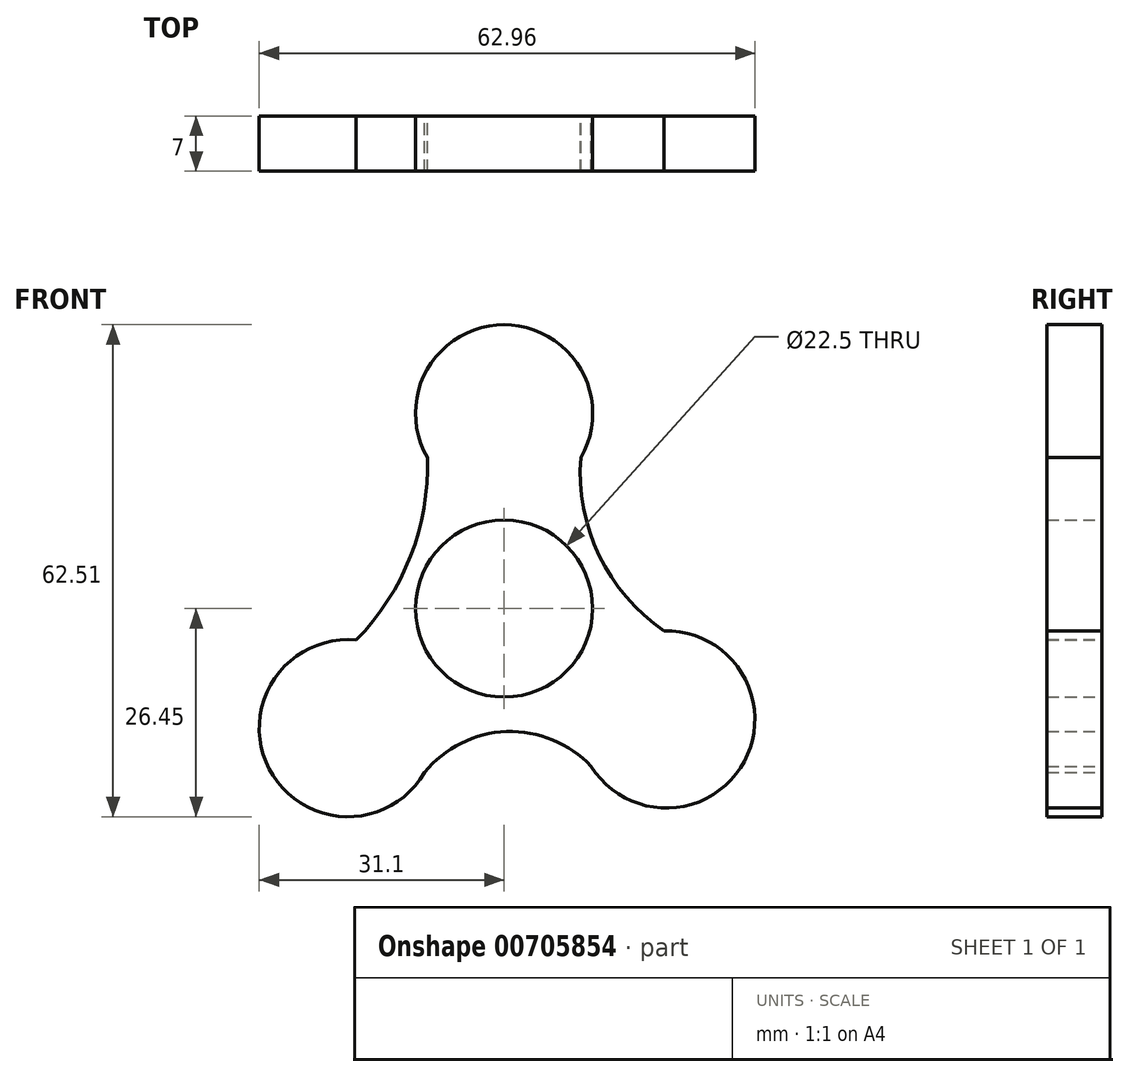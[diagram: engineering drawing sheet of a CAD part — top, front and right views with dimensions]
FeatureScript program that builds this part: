
annotation { "Feature Type Name" : "Feature", "Feature Type Description" : "" }
export const myFeature = defineFeature(function(context is Context, id is Id, definition is map)
    precondition{}
    {
        {
            var Q0;
            Q0=qCreatedBy(makeId("Front.planeOp"),FACE);
            var sketch = newSketch(context, id + "F0", { "sketchPlane" : qUnion([Q0])});
            skCircle(sketch, "E0", {"center": v(0, 0) * mm, "radius": 11.25 * mm});
            skCircle(sketch, "E1", {"center": v(0, 24.8) * mm, "radius": 11.25 * mm});
            skCircle(sketch, "E2", {"center": v(20.6, -14.08) * mm, "radius": 11.25 * mm});
            skCircle(sketch, "E3", {"center": v(-19.85, -15.2) * mm, "radius": 11.25 * mm});
            skLineSegment(sketch, "E4", {"start": v(0, 24.8) * mm, "end": v(0, 41.12) * mm});
            skLineSegment(sketch, "E5", {"start": v(0, 24.8) * mm, "end": v(17.45, 14.73) * mm});
            skLineSegment(sketch, "E6", {"start": v(0, 24.8) * mm, "end": v(-15.27, 15.99) * mm});
            skLineSegment(sketch, "E7", {"start": v(-19.85, -15.2) * mm, "end": v(-19.85, 5.14) * mm});
            skLineSegment(sketch, "E8", {"start": v(-19.85, -15.2) * mm, "end": v(-37.06, -28.16) * mm});
            skLineSegment(sketch, "E9", {"start": v(-19.85, -15.2) * mm, "end": v(-4.02, -24.34) * mm});
            skLineSegment(sketch, "E10", {"start": v(20.6, -14.08) * mm, "end": v(20.6, 8.04) * mm});
            skLineSegment(sketch, "E11", {"start": v(20.6, -14.08) * mm, "end": v(38.26, -24.28) * mm});
            skLineSegment(sketch, "E12", {"start": v(20.6, -14.08) * mm, "end": v(7.87, -26.6) * mm});
            skArc(sketch, "E13", {"start": v(-19.85, -5.03) * mm, "mid": v(-12.16, 5.97) * mm, "end": v(-9.74, 19.18) * mm});
            skArc(sketch, "E14", {"start": v(9.74, 19.18) * mm, "mid": v(12.16, 6.6) * mm, "end": v(20.6, -3.02) * mm});
            skArc(sketch, "E15", {"start": v(12.58, -21.97) * mm, "mid": v(1.53, -15.64) * mm, "end": v(-10.1, -20.83) * mm});
            skSolve(sketch);
        }
        {
            var Q0;
            Q0 = qSketchRegion(id + "F0", true);
            extrude(context, id + "F1", {"entities" : qUnion([Q0]), "depth" : 7 * mm, "offsetDistance" : 25 * mm});
        }
    });
